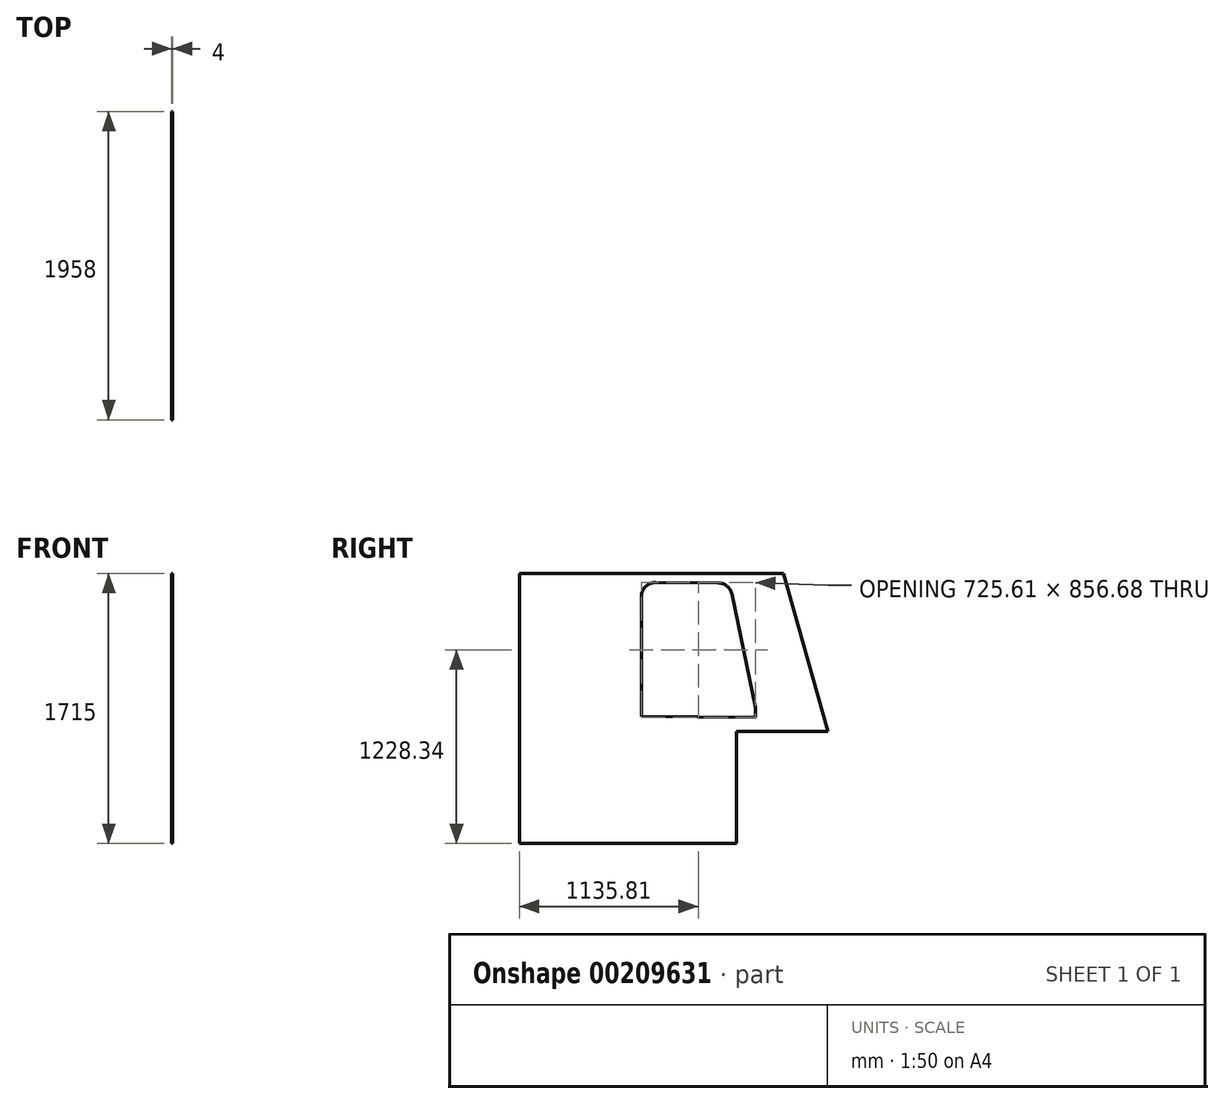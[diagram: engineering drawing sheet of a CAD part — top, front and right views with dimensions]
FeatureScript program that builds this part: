
annotation { "Feature Type Name" : "Feature", "Feature Type Description" : "" }
export const myFeature = defineFeature(function(context is Context, id is Id, definition is map)
    precondition{}
    {
        {
            var Q0;
            Q0=qCreatedBy(makeId("Right.planeOp"),FACE);
            var sketch = newSketch(context, id + "F0", { "sketchPlane" : qUnion([Q0])});
            skLineSegment(sketch, "E0.bottom", {"start": v(979, -857.5) * mm, "end": v(-979, -857.5) * mm});
            skLineSegment(sketch, "E0.top", {"start": v(979, 857.5) * mm, "end": v(-979, 857.5) * mm});
            skLineSegment(sketch, "E0.left", {"start": v(979, -857.5) * mm, "end": v(979, 857.5) * mm});
            skLineSegment(sketch, "E0.right", {"start": v(-979, -857.5) * mm, "end": v(-979, 857.5) * mm});
            skPoint(sketch, "E0.middle", {"position": v(0, 0) * mm});
            skSolve(sketch);
        }
        {
            var Q0;
            Q0 = qSketchRegion(id + "F0", true);
            extrude(context, id + "F1", {"entities" : qUnion([Q0]), "depth" : 4 * mm});
        }
        {
            var Q0;
            Q0=makeQuery(id+"F1.opExtrude","CAP_FACE",FACE,{"disambiguationData":[OSD([sQuery(id+"F0.wireOp",EDGE,"E0.bottom"),sQuery(id+"F0.wireOp",EDGE,"E0.top"),sQuery(id+"F0.wireOp",EDGE,"E0.left"),sQuery(id+"F0.wireOp",EDGE,"E0.right")])],"isStart":false});
            var sketch = newSketch(context, id + "F2", { "sketchPlane" : qUnion([Q0])});
            skLineSegment(sketch, "E1", {"start": v(979, -147.5) * mm, "end": v(697, 857.5) * mm});
            skLineSegment(sketch, "E2", {"start": v(697, 857.5) * mm, "end": v(979, 857.5) * mm});
            skLineSegment(sketch, "E3", {"start": v(979, 857.5) * mm, "end": v(979, -147.5) * mm});
            skLineSegment(sketch, "E4.bottom", {"start": v(979, -147.5) * mm, "end": v(397, -147.5) * mm});
            skLineSegment(sketch, "E4.top", {"start": v(979, -857.5) * mm, "end": v(397, -857.5) * mm});
            skLineSegment(sketch, "E4.left", {"start": v(979, -147.5) * mm, "end": v(979, -857.5) * mm});
            skLineSegment(sketch, "E4.right", {"start": v(397, -147.5) * mm, "end": v(397, -857.5) * mm});
            skSolve(sketch);
        }
        {
            var Q0;
            Q0 = qSketchRegion(id + "F2", true);
            extrude(context, id + "F3", {"entities" : qUnion([Q0]), "operationType" : NewBodyOperationType.REMOVE, "endBound" : BoundingType.THROUGH_ALL, "oppositeDirection" : true, "depth" : 25 * mm});
        }
        {
            var Q0;
            Q0=makeQuery(id+"F1.opExtrude","CAP_FACE",FACE,{"disambiguationData":[OSD([sQuery(id+"F0.wireOp",EDGE,"E0.bottom"),sQuery(id+"F0.wireOp",EDGE,"E0.top"),sQuery(id+"F0.wireOp",EDGE,"E0.left"),sQuery(id+"F0.wireOp",EDGE,"E0.right")])],"isStart":false});
            var sketch = newSketch(context, id + "F4", { "sketchPlane" : qUnion([Q0])});
            skLineSegment(sketch, "E5", {"start": v(-206, 799.5) * mm, "end": v(-206, -52.5) * mm});
            skLineSegment(sketch, "E6", {"start": v(-206, 799.5) * mm, "end": v(353.6, 797.5) * mm});
            skLineSegment(sketch, "E7", {"start": v(519.61, -57.5) * mm, "end": v(-206, -52.5) * mm});
            skLineSegment(sketch, "E8", {"start": v(519.61, 7.5) * mm, "end": v(519.61, -57.5) * mm});
            skLineSegment(sketch, "E9", {"start": v(353.6, 797.5) * mm, "end": v(519.61, 7.5) * mm});
            skLineSegment(sketch, "E10", {"start": v(353.6, 797.5) * mm, "end": v(341, 857.5) * mm, "construction": true});
            skPoint(sketch, "E11", {"position": v(482, 186.5) * mm});
            skSolve(sketch);
        }
        {
            var Q0;
            Q0 = qSketchRegion(id + "F4", true);
            extrude(context, id + "F5", {"entities" : qUnion([Q0]), "operationType" : NewBodyOperationType.REMOVE, "endBound" : BoundingType.THROUGH_ALL, "oppositeDirection" : true, "depth" : 25 * mm});
        }
        {
            var Q0;
            Q0=makeQuery(id+"F5.boolean.opBoolean","COPY",EDGE,{"derivedFrom":makeQuery(id+"F5.opExtrude","SWEPT_EDGE",EDGE,{"disambiguationData":[OSD([sQuery(id+"F4.wireOp",EDGE,"E5"),sQuery(id+"F4.wireOp",EDGE,"E6")])]})});
            var Q1;
            Q1=makeQuery(id+"F5.boolean.opBoolean","COPY",EDGE,{"derivedFrom":makeQuery(id+"F5.opExtrude","SWEPT_EDGE",EDGE,{"disambiguationData":[OSD([sQuery(id+"F4.wireOp",EDGE,"E6"),sQuery(id+"F4.wireOp",EDGE,"E9")])]})});
            fillet(context, id + "F6", {"entities" : qUnion([Q0, Q1]), "radius" : 90 * mm, "tangentPropagation" : true, "allowEdgeOverflow" : false});
        }
    });
